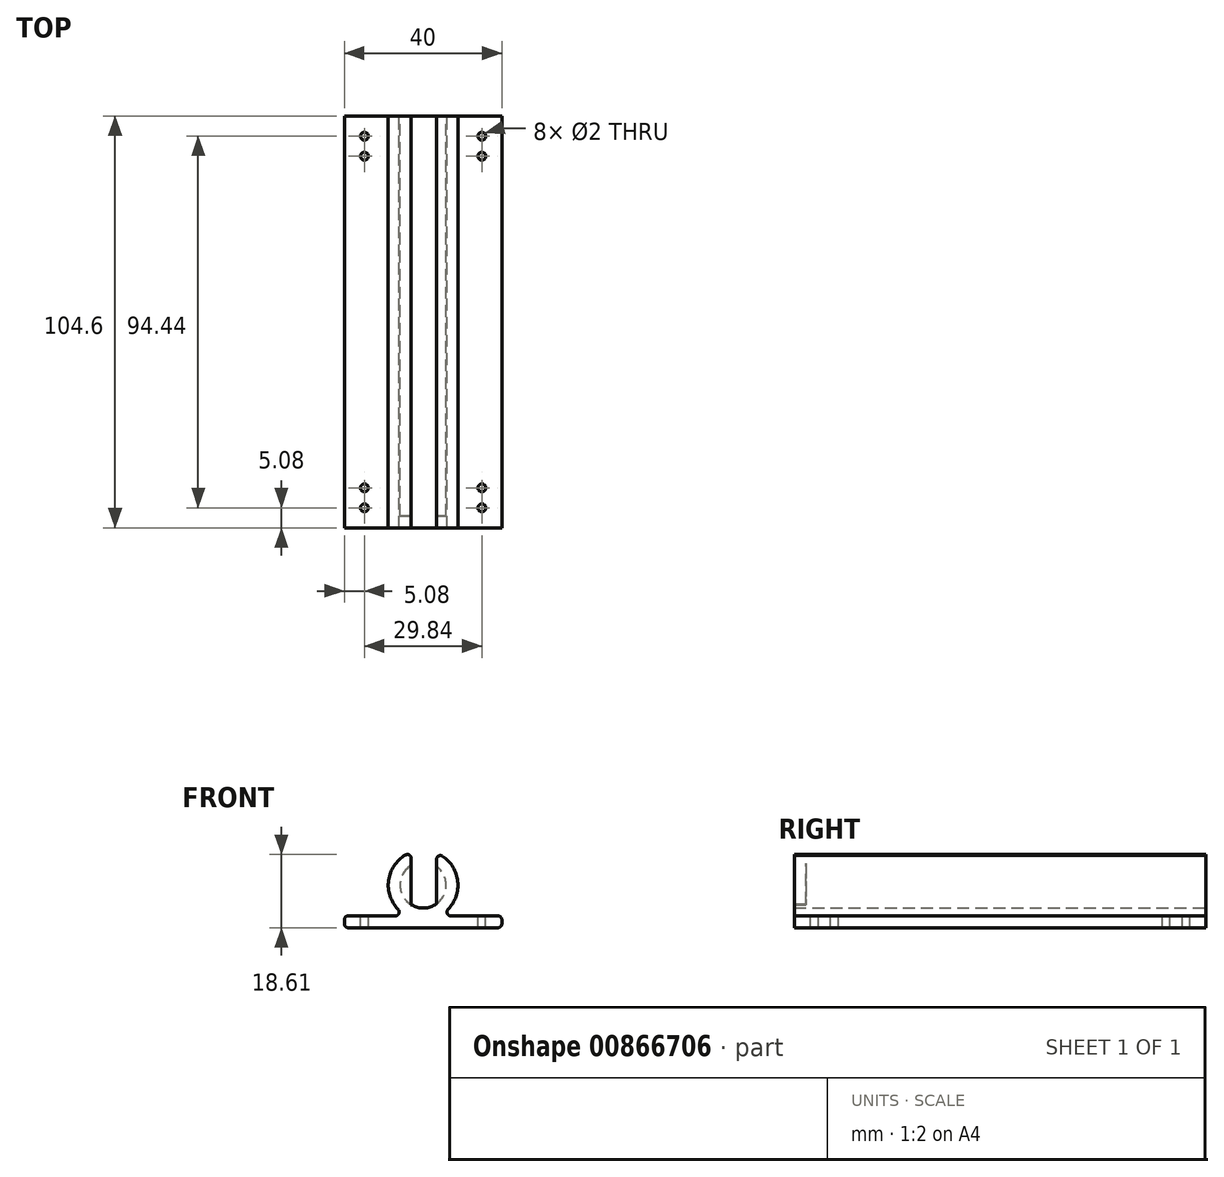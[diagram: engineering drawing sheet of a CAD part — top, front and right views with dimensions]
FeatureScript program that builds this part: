
annotation { "Feature Type Name" : "Feature", "Feature Type Description" : "" }
export const myFeature = defineFeature(function(context is Context, id is Id, definition is map)
    precondition{}
    {
        {
            var Q0;
            Q0=qCreatedBy(makeId("Front.planeOp"),FACE);
            var sketch = newSketch(context, id + "F0", { "sketchPlane" : qUnion([Q0])});
            skArc(sketch, "E0", {"start": v(-3, 5.02) * mm, "mid": v(-0.25, -5.85) * mm, "end": v(3.42, 4.75) * mm});
            skArc(sketch, "E1", {"start": v(-3, 8.33) * mm, "mid": v(-8.83, 0.6) * mm, "end": v(-4.09, -7.85) * mm});
            skLineSegment(sketch, "E2", {"start": v(-3, 5.02) * mm, "end": v(-3, 8.33) * mm});
            skLineSegment(sketch, "E3", {"start": v(3.42, 4.75) * mm, "end": v(3.42, 8.17) * mm});
            skPoint(sketch, "E4.orphan", {"position": v(-3, 4.33) * mm});
            skLineSegment(sketch, "E5.bottom", {"start": v(-20, -7.85) * mm, "end": v(-4.09, -7.85) * mm});
            skLineSegment(sketch, "E5.top", {"start": v(-20, -10.85) * mm, "end": v(20, -10.85) * mm});
            skLineSegment(sketch, "E5.left", {"start": v(-20, -7.85) * mm, "end": v(-20, -10.85) * mm});
            skLineSegment(sketch, "E5.right", {"start": v(20, -7.85) * mm, "end": v(20, -10.85) * mm});
            skLineSegment(sketch, "E6.trimOffspring", {"start": v(4.09, -7.85) * mm, "end": v(20, -7.85) * mm});
            skArc(sketch, "E7.trimOffspring", {"start": v(4.09, -7.85) * mm, "mid": v(8.84, 0.37) * mm, "end": v(3.42, 8.17) * mm});
            skPoint(sketch, "E8.visualSharp", {"position": v(-20, -7.85) * mm});
            skLineSegment(sketch, "E8.filletArc", {"start": v(-20, -7.85) * mm, "end": v(-20, -7.85) * mm});
            skPoint(sketch, "E9.visualSharp", {"position": v(-20, -10.85) * mm});
            skLineSegment(sketch, "E9.filletArc", {"start": v(-20, -10.85) * mm, "end": v(-20, -10.85) * mm});
            skPoint(sketch, "E10.visualSharp", {"position": v(20, -7.85) * mm});
            skLineSegment(sketch, "E10.filletArc", {"start": v(20, -7.85) * mm, "end": v(20, -7.85) * mm});
            skPoint(sketch, "E11.visualSharp", {"position": v(20, -10.85) * mm});
            skLineSegment(sketch, "E11.filletArc", {"start": v(20, -10.85) * mm, "end": v(20, -10.85) * mm});
            skPoint(sketch, "E12.visualSharp", {"position": v(-3, 8.33) * mm});
            skLineSegment(sketch, "E12.filletArc", {"start": v(-3, 8.33) * mm, "end": v(-3, 8.33) * mm});
            skPoint(sketch, "E13.visualSharp", {"position": v(3.42, 8.17) * mm});
            skLineSegment(sketch, "E13.filletArc", {"start": v(3.42, 8.17) * mm, "end": v(3.42, 8.17) * mm});
            skPoint(sketch, "E14.visualSharp", {"position": v(-3, 5.02) * mm});
            skLineSegment(sketch, "E14.filletArc", {"start": v(-3, 5.02) * mm, "end": v(-3, 5.02) * mm});
            skPoint(sketch, "E15.visualSharp", {"position": v(3.42, 4.75) * mm});
            skLineSegment(sketch, "E15.filletArc", {"start": v(3.42, 4.75) * mm, "end": v(3.42, 4.75) * mm});
            skPoint(sketch, "E16.visualSharp", {"position": v(-4.09, -7.85) * mm});
            skLineSegment(sketch, "E16.filletArc", {"start": v(-4.09, -7.85) * mm, "end": v(-4.09, -7.85) * mm});
            skPoint(sketch, "E17.visualSharp", {"position": v(4.09, -7.85) * mm});
            skLineSegment(sketch, "E17.filletArc", {"start": v(4.09, -7.85) * mm, "end": v(4.09, -7.85) * mm});
            skSolve(sketch);
        }
        {
            var Q0;
            Q0=makeQuery(id+"F0.imprint","IMPRINT",FACE,{"disambiguationData":[TD([[makeQuery(id+"F0.imprint","IMPRINT",EDGE,{"derivedFrom":sQuery(id+"F0.wireOp",EDGE,"E0")}),-1.0]])]});
            extrude(context, id + "F1", {"entities" : qUnion([Q0]), "depth" : 101.6 * mm, "offsetDistance" : 25.4 * mm});
        }
        {
            var Q0;
            Q0=makeQuery(id+"F1.opExtrude","CAP_FACE",FACE,{"disambiguationData":[OSD([sQuery(id+"F0.wireOp",EDGE,"E0"),sQuery(id+"F0.wireOp",EDGE,"E1"),sQuery(id+"F0.wireOp",EDGE,"E2"),sQuery(id+"F0.wireOp",EDGE,"E3"),sQuery(id+"F0.wireOp",EDGE,"E5.bottom"),sQuery(id+"F0.wireOp",EDGE,"E5.top"),sQuery(id+"F0.wireOp",EDGE,"E5.left"),sQuery(id+"F0.wireOp",EDGE,"E5.right"),sQuery(id+"F0.wireOp",EDGE,"E6.trimOffspring"),sQuery(id+"F0.wireOp",EDGE,"E7.trimOffspring")])],"isStart":false});
            var sketch = newSketch(context, id + "F2", { "sketchPlane" : qUnion([Q0])});
            skArc(sketch, "E18.0", {"start": v(-3, 8.33) * mm, "mid": v(-8.83, 0.6) * mm, "end": v(-4.09, -7.85) * mm});
            skArc(sketch, "E18.1", {"start": v(4.09, -7.85) * mm, "mid": v(8.84, 0.37) * mm, "end": v(3.42, 8.17) * mm});
            skLineSegment(sketch, "E18.2", {"start": v(4.09, -7.85) * mm, "end": v(20, -7.85) * mm});
            skLineSegment(sketch, "E18.3", {"start": v(-20, -7.85) * mm, "end": v(-4.09, -7.85) * mm});
            skLineSegment(sketch, "E18.4", {"start": v(-20, -7.85) * mm, "end": v(-20, -10.85) * mm});
            skLineSegment(sketch, "E18.5", {"start": v(-20, -10.85) * mm, "end": v(20, -10.85) * mm});
            skLineSegment(sketch, "E18.6", {"start": v(20, -7.85) * mm, "end": v(20, -10.85) * mm});
            skLineSegment(sketch, "E19", {"start": v(-3, 8.33) * mm, "end": v(-3, -5.02) * mm});
            skLineSegment(sketch, "E20", {"start": v(3.42, 8.17) * mm, "end": v(3.42, -4.75) * mm});
            skArc(sketch, "E21.0", {"start": v(-3, -5.02) * mm, "mid": v(0.25, -5.85) * mm, "end": v(3.42, -4.75) * mm});
            skPoint(sketch, "E22.orphan", {"position": v(-3, 5.02) * mm});
            skPoint(sketch, "E23.orphan", {"position": v(3.42, 4.75) * mm});
            skSolve(sketch);
        }
        {
            var Q0;
            Q0 = qSketchRegion(id + "F2", true);
            extrude(context, id + "F3", {"entities" : qUnion([Q0]), "operationType" : NewBodyOperationType.ADD, "depth" : 3 * mm, "offsetDistance" : 25.4 * mm});
        }
        {
            var Q0;
            Q0=qCreatedBy(makeId("Top.planeOp"),FACE);
            var sketch = newSketch(context, id + "F4", { "sketchPlane" : qUnion([Q0])});
            skCircle(sketch, "E24", {"center": v(-14.92, -5.08) * mm, "radius": 1 * mm});
            skCircle(sketch, "E25", {"center": v(-14.92, -10.16) * mm, "radius": 1 * mm});
            skCircle(sketch, "E26", {"center": v(-14.92, -99.52) * mm, "radius": 1 * mm});
            skCircle(sketch, "E27", {"center": v(-14.92, -94.44) * mm, "radius": 1 * mm});
            skCircle(sketch, "E28.MirrorC", {"center": v(14.92, -99.52) * mm, "radius": 1 * mm});
            skCircle(sketch, "E29.MirrorC", {"center": v(14.92, -94.44) * mm, "radius": 1 * mm});
            skCircle(sketch, "E30.MirrorC", {"center": v(14.92, -10.16) * mm, "radius": 1 * mm});
            skCircle(sketch, "E31.MirrorC", {"center": v(14.92, -5.08) * mm, "radius": 1 * mm});
            skSolve(sketch);
        }
        {
            var Q0;
            Q0 = qSketchRegion(id + "F4", true);
            extrude(context, id + "F5", {"entities" : qUnion([Q0]), "operationType" : NewBodyOperationType.REMOVE, "oppositeDirection" : true, "depth" : 25.4 * mm, "offsetDistance" : 25.4 * mm});
        }
        {
            var Q0;
            Q0=makeQuery(id+"F3.boolean.opBoolean","MERGE",EDGE,{"derivedFrom":[makeQuery(id+"F1.opExtrude","SWEPT_EDGE",EDGE,{"disambiguationData":[OSD([sQuery(id+"F0.wireOp",EDGE,"E1"),sQuery(id+"F0.wireOp",EDGE,"E2")])]}),makeQuery(id+"F3.opExtrude","SWEPT_EDGE",EDGE,{"disambiguationData":[OSD([sQuery(id+"F2.wireOp",EDGE,"E18.0"),sQuery(id+"F2.wireOp",EDGE,"E19")])]})]});
            var Q1;
            Q1=makeQuery(id+"F3.boolean.opBoolean","MERGE",EDGE,{"derivedFrom":[makeQuery(id+"F1.opExtrude","SWEPT_EDGE",EDGE,{"disambiguationData":[OSD([sQuery(id+"F0.wireOp",EDGE,"E3"),sQuery(id+"F0.wireOp",EDGE,"E7.trimOffspring")])]}),makeQuery(id+"F3.opExtrude","SWEPT_EDGE",EDGE,{"disambiguationData":[OSD([sQuery(id+"F2.wireOp",EDGE,"E18.1"),sQuery(id+"F2.wireOp",EDGE,"E20")])]})]});
            var Q2;
            Q2=makeQuery(id+"F1.opExtrude","SWEPT_EDGE",EDGE,{"disambiguationData":[OSD([sQuery(id+"F0.wireOp",EDGE,"E0"),sQuery(id+"F0.wireOp",EDGE,"E2")])]});
            var Q3;
            Q3=makeQuery(id+"F1.opExtrude","SWEPT_EDGE",EDGE,{"disambiguationData":[OSD([sQuery(id+"F0.wireOp",EDGE,"E0"),sQuery(id+"F0.wireOp",EDGE,"E3")])]});
            fillet(context, id + "F6", {"entities" : qUnion([Q0, Q1, Q2, Q3]), "radius" : 1 * mm, "tangentPropagation" : true, "allowEdgeOverflow" : false});
        }
        {
            var Q0;
            Q0=makeQuery(id+"F3.boolean.opBoolean","MERGE",EDGE,{"derivedFrom":[makeQuery(id+"F1.opExtrude","SWEPT_EDGE",EDGE,{"disambiguationData":[OSD([sQuery(id+"F0.wireOp",EDGE,"E5.right"),sQuery(id+"F0.wireOp",EDGE,"E6.trimOffspring")])]}),makeQuery(id+"F3.opExtrude","SWEPT_EDGE",EDGE,{"disambiguationData":[OSD([sQuery(id+"F2.wireOp",EDGE,"E18.2"),sQuery(id+"F2.wireOp",EDGE,"E18.6")])]})]});
            var Q1;
            Q1=makeQuery(id+"F3.boolean.opBoolean","MERGE",EDGE,{"derivedFrom":[makeQuery(id+"F1.opExtrude","SWEPT_EDGE",EDGE,{"disambiguationData":[OSD([sQuery(id+"F0.wireOp",EDGE,"E5.top"),sQuery(id+"F0.wireOp",EDGE,"E5.right")])]}),makeQuery(id+"F3.opExtrude","SWEPT_EDGE",EDGE,{"disambiguationData":[OSD([sQuery(id+"F2.wireOp",EDGE,"E18.5"),sQuery(id+"F2.wireOp",EDGE,"E18.6")])]})]});
            var Q2;
            Q2=makeQuery(id+"F3.boolean.opBoolean","MERGE",EDGE,{"derivedFrom":[makeQuery(id+"F1.opExtrude","SWEPT_EDGE",EDGE,{"disambiguationData":[OSD([sQuery(id+"F0.wireOp",EDGE,"E5.bottom"),sQuery(id+"F0.wireOp",EDGE,"E5.left")])]}),makeQuery(id+"F3.opExtrude","SWEPT_EDGE",EDGE,{"disambiguationData":[OSD([sQuery(id+"F2.wireOp",EDGE,"E18.3"),sQuery(id+"F2.wireOp",EDGE,"E18.4")])]})]});
            var Q3;
            Q3=makeQuery(id+"F3.boolean.opBoolean","MERGE",EDGE,{"derivedFrom":[makeQuery(id+"F1.opExtrude","SWEPT_EDGE",EDGE,{"disambiguationData":[OSD([sQuery(id+"F0.wireOp",EDGE,"E5.top"),sQuery(id+"F0.wireOp",EDGE,"E5.left")])]}),makeQuery(id+"F3.opExtrude","SWEPT_EDGE",EDGE,{"disambiguationData":[OSD([sQuery(id+"F2.wireOp",EDGE,"E18.4"),sQuery(id+"F2.wireOp",EDGE,"E18.5")])]})]});
            var Q4;
            Q4=makeQuery(id+"F3.boolean.opBoolean","MERGE",EDGE,{"derivedFrom":[makeQuery(id+"F1.opExtrude","SWEPT_EDGE",EDGE,{"disambiguationData":[OSD([sQuery(id+"F0.wireOp",EDGE,"E6.trimOffspring"),sQuery(id+"F0.wireOp",EDGE,"E7.trimOffspring")])]}),makeQuery(id+"F3.opExtrude","SWEPT_EDGE",EDGE,{"disambiguationData":[OSD([sQuery(id+"F2.wireOp",EDGE,"E18.1"),sQuery(id+"F2.wireOp",EDGE,"E18.2")])]})]});
            var Q5;
            Q5=makeQuery(id+"F3.boolean.opBoolean","MERGE",EDGE,{"derivedFrom":[makeQuery(id+"F1.opExtrude","SWEPT_EDGE",EDGE,{"disambiguationData":[OSD([sQuery(id+"F0.wireOp",EDGE,"E1"),sQuery(id+"F0.wireOp",EDGE,"E5.bottom")])]}),makeQuery(id+"F3.opExtrude","SWEPT_EDGE",EDGE,{"disambiguationData":[OSD([sQuery(id+"F2.wireOp",EDGE,"E18.0"),sQuery(id+"F2.wireOp",EDGE,"E18.3")])]})]});
            fillet(context, id + "F7", {"entities" : qUnion([Q0, Q1, Q2, Q3, Q4, Q5]), "radius" : 1 * mm, "tangentPropagation" : true, "allowEdgeOverflow" : false});
        }
    });
